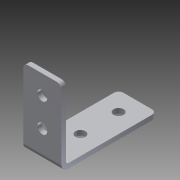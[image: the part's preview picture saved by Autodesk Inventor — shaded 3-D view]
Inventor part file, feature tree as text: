
AUTODESK INVENTOR PART (.ipt)
format: ipt  version: 2014 SP1 (Build 180222100, 222)  size: 183,808 bytes
history: native  units: in
note: dims shown in document units (in); Inventor stores cm internally (conversion verified against a paired STEP export)
features: other x4, sheet_metal_op x3, sketch x3, chamfer x1
ambient origin geometry x8: Origin, YZ Plane, XZ Plane, XY Plane, X Axis, Y Axis, Z Axis, Center Point
bodies: Solid1 (feature_tree)
feature tree (11):
  sheet_metal_op  "Face1"
  sheet_metal_op  "Flange1"
  chamfer  "Corner Round1"
  sketch  "Sketch1"  dims[d0=0.26in]
  other  "Plate1"
  sketch  "Sketch2"  dims[d2=1.0in]
  other  "Plate2"
  sheet_metal_op  "Bend1"
  sketch  "Sketch3"  dims[d3=2.5in d4=1.0in d5=1.0in d6=0.125in d7=0.125in d8=0.0625in d9=0.25in d10=0.125in d11=2.0in d12=90.0deg d13=0.05in d14=0.5in d15=0.125in d16=0.125in d17=0.75in d18=0.75in d19=0.26in d20=0.125in d21=0.0in d22=0.125in]
  other  "Cut1"
  other  "Definition1"
